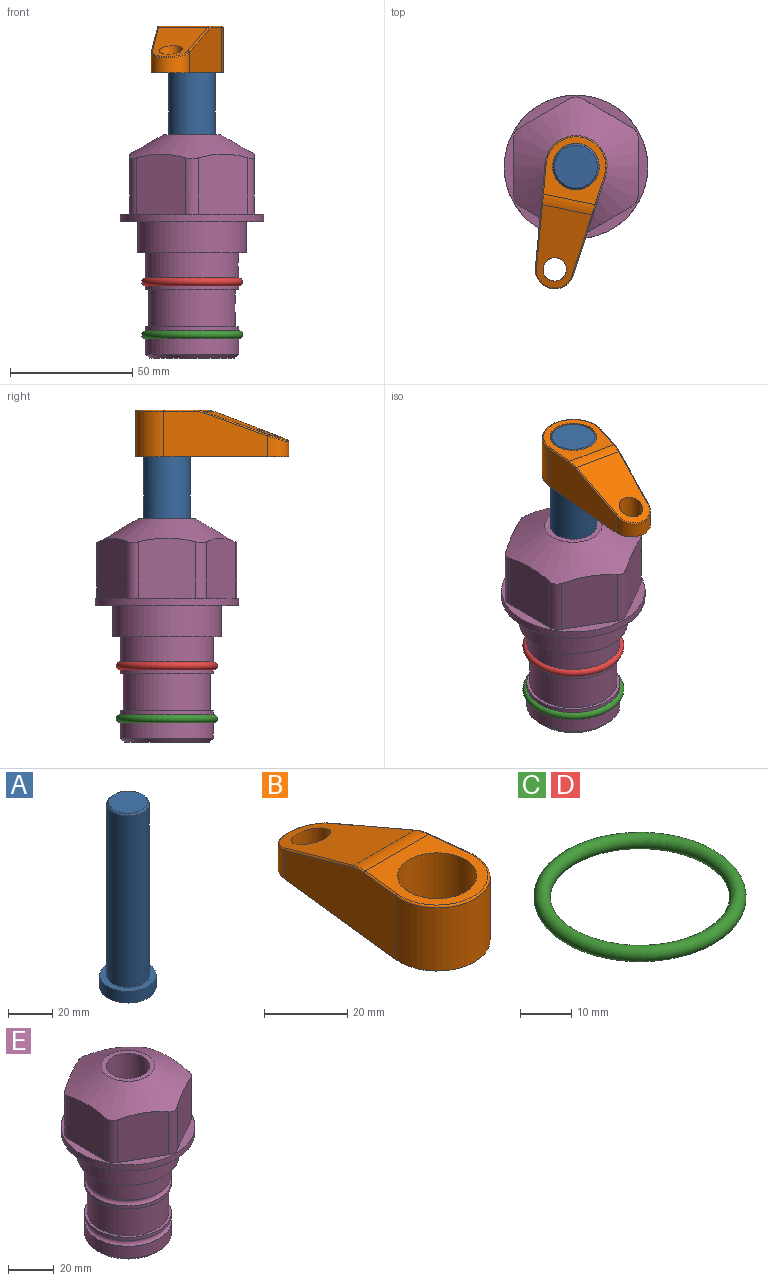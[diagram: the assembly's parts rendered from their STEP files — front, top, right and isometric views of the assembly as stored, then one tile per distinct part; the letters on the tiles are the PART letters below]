
ASSEMBLY  parts=5 mates=3
PART A: 6 faces, bbox 25.4x25.4x101.6 mm
  f0: plane 17.46x17.46mm, normal (0,0,1), area 239.5mm2, adj f5
  f1: plane 25.4x25.4mm, normal (0,0,-1), area 506.7mm2, adj f2
  f2: cylinder r=12.7mm len=25.4mm, axis (0,0,1), area 506.7mm2, adj f1,f3
  f3: plane 25.4x25.4mm, normal (0,0,1), area 221.7mm2, adj f2,f4
  f4: cylinder r=9.53mm len=94.46mm, axis (0,0,1), area 5653mm2, adj f3,f5
  f5: cone r=8.73mm half-angle=45deg, axis (0,0,-1), area 64.4mm2, adj f0,f4
PART B: 44 faces, bbox 27.5x64.5x19.1 mm
  f0: plane 2.3x0.95mm, normal (0,0,-1), area 1mm2, adj f25,f30,f34
  f1: plane 63.5x25.4mm, normal (0,0,-1), area 561.7mm2, adj f2,f3,f4,f5,f6,f7,f19,f20
  f2: cylinder r=12.7mm len=25.4mm, axis (0,0,-1), area 792.2mm2, adj f1,f3,f5,f13
  f3: plane 42.33x18.54mm, normal (0.99,0.11,0), area 647mm2, adj f1,f2,f4,f11,f12,f14
  f4: cylinder r=7.94mm len=15.78mm, axis (0,0,-1), area 158.6mm2, adj f1,f3,f5,f16
  f5: plane 42.33x18.54mm, normal (-0.99,0.11,0), area 647mm2, adj f1,f2,f4,f15,f17,f18
  f6: cylinder r=9.53mm len=19.05mm, axis (0,0,-1), area 1140.1mm2, adj f1,f8
  f7: cylinder r=4.76mm len=10.98mm, axis (0,0,-1), area 276.1mm2, adj f1,f9
  f8: plane 25.83x24.38mm, normal (0,0,1), area 262.2mm2, adj f6,f10,f11,f13,f15
  f9: plane 32.49x20.55mm, normal (0,0.34,0.94), area 489.9mm2, adj f7,f10,f14,f16,f18
  f10: cylinder r=12.7mm len=21.49mm, axis (-1,0,0), area 93.2mm2, adj f8,f9,f12,f17
  f11: cylinder r=0.51mm len=12.34mm, axis (0.11,-0.99,0), area 9.9mm2, adj f3,f8,f12,f13
  f12: bspline ~7.62x1.64mm, area 3.5mm2, adj f3,f10,f11,f14
  f13: torus R=12.19mm, axis (0,0,1), area 33.6mm2, adj f2,f8,f11,f15
  f14: cylinder r=0.51mm len=26.01mm, axis (0.1,-0.93,0.34), area 21.6mm2, adj f3,f9,f12,f16
  f15: cylinder r=0.51mm len=12.34mm, axis (0.11,0.99,0), area 9.9mm2, adj f5,f8,f13,f17
  f16: bspline ~15.78x7.05mm, area 15.7mm2, adj f4,f9,f14,f18
  f17: bspline ~7.62x1.64mm, area 3.5mm2, adj f5,f10,f15,f18
  f18: cylinder r=0.51mm len=26.01mm, axis (0.1,0.93,-0.34), area 21.6mm2, adj f5,f9,f16,f17
  f19: plane 21.6x14.29mm, normal (-0.99,-0.11,0), area 242.6mm2, adj f1,f26,f28,f34,f36,f38
  f20: plane 21.6x14.29mm, normal (0.99,-0.11,0), area 242.6mm2, adj f1,f27,f29,f37,f39,f41
  f21: cylinder r=12.7mm len=14.29mm, axis (0,0,-1), area 173.2mm2, adj f1,f26,f27,f30,f31,f33
  f22: cylinder r=7.94mm len=7.63mm, axis (0,0,-1), area 53.8mm2, adj f1,f28,f29,f42
  f23: plane 2.3x0.95mm, normal (0,0,-1), area 1mm2, adj f25,f33,f37
  f24: plane 17.94x12.32mm, normal (0,-0.34,-0.94), area 191.2mm2, adj f25,f38,f41,f42
  f25: cylinder r=9.53mm len=12.93mm, axis (-1,0,0), area 37.5mm2, adj f0,f23,f24,f31,f36,f39
  f26: cylinder r=1.59mm len=14.29mm, axis (0,0,-1), area 49mm2, adj f1,f19,f21,f32
  f27: cylinder r=1.59mm len=14.29mm, axis (0,0,-1), area 49mm2, adj f1,f20,f21,f35
  f28: cylinder r=1.59mm len=7.28mm, axis (0,0,-1), area 22.1mm2, adj f1,f19,f22,f40
  f29: cylinder r=1.59mm len=7.28mm, axis (0,0,-1), area 22.1mm2, adj f1,f20,f22,f43
  f30: torus R=14.29mm, axis (0,0,1), area 5.8mm2, adj f0,f21,f31,f32
  f31: bspline ~11.06x2.73mm, area 20.8mm2, adj f21,f25,f30,f33
  f32: sphere r=1.59mm, area 5.4mm2, adj f26,f30,f34
  f33: torus R=14.29mm, axis (0,0,1), area 5.8mm2, adj f21,f23,f31,f35
  f34: cylinder r=1.59mm len=1.68mm, axis (-0.11,0.99,0), area 2.4mm2, adj f0,f19,f32,f36
  f35: sphere r=1.59mm, area 5.4mm2, adj f27,f33,f37
  f36: bspline ~5.82x2.33mm, area 7.7mm2, adj f19,f25,f34,f38
  f37: cylinder r=1.59mm len=1.68mm, axis (0.11,0.99,0), area 2.4mm2, adj f20,f23,f35,f39
  f38: cylinder r=1.59mm len=18.33mm, axis (0.1,-0.93,0.34), area 46.7mm2, adj f19,f24,f36,f40
  f39: bspline ~5.82x2.33mm, area 7.7mm2, adj f20,f25,f37,f41
  f40: sphere r=1.59mm, area 3.6mm2, adj f28,f38,f42
  f41: cylinder r=1.59mm len=18.33mm, axis (0.1,0.93,-0.34), area 46.7mm2, adj f20,f24,f39,f43
  f42: bspline ~8.31x1.84mm, area 15.3mm2, adj f22,f24,f40,f43
  f43: sphere r=1.59mm, area 3.6mm2, adj f29,f41,f42
PART C: 1 faces, bbox 44.7x44.7x3.2 mm
  f0: torus R=19.05mm, axis (0,0,1), area 1193.9mm2
PART D: same geometry as C
PART E: 36 faces, bbox 58.7x58.7x91.2 mm
  f0: cylinder r=17.78mm len=35.56mm, axis (0,0,1), area 1670.8mm2, adj f23,f24,f31
  f1: cylinder r=19.05mm len=38.1mm, axis (0,0,1), area 1191.9mm2, adj f26,f27,f30
  f2: plane 58.66x58.66mm, normal (0,0,-1), area 1150.6mm2, adj f3,f28
  f3: cylinder r=29.33mm len=58.66mm, axis (0,0,-1), area 585.1mm2, adj f2,f4
  f4: plane 58.66x58.66mm, normal (0,0,1), area 475.9mm2, adj f3,f5,f6,f7,f8,f9,f10,f11
  f5: plane 24.5x20.32mm, normal (0.5,-0.87,0), area 562.8mm2, adj f4,f15,f16,f17
  f6: plane 24.5x20.32mm, normal (-0.5,-0.87,0), area 562.8mm2, adj f4,f14,f15,f17
  f7: plane 24.5x23.48mm, normal (-1,0,0), area 562.8mm2, adj f4,f13,f14,f17
  f8: plane 24.5x20.32mm, normal (-0.5,0.87,0), area 562.8mm2, adj f4,f12,f13,f17
  f9: plane 24.5x20.32mm, normal (0.5,0.87,0), area 562.8mm2, adj f4,f11,f12,f17
  f10: plane 24.5x23.48mm, normal (1,0,0), area 562.8mm2, adj f4,f11,f16,f17
  f11: cylinder r=5.08mm len=23.01mm, axis (0,0,-1), area 121.2mm2, adj f4,f9,f10,f17
  f12: cylinder r=5.08mm len=23.01mm, axis (0,0,-1), area 121.2mm2, adj f4,f8,f9,f17
  f13: cylinder r=5.08mm len=23.01mm, axis (0,0,-1), area 121.2mm2, adj f4,f7,f8,f17
  f14: cylinder r=5.08mm len=23.01mm, axis (0,0,-1), area 121.2mm2, adj f4,f6,f7,f17
  f15: cylinder r=5.08mm len=23.01mm, axis (0,0,-1), area 121.2mm2, adj f4,f5,f6,f17
  f16: cylinder r=5.08mm len=23.01mm, axis (0,0,-1), area 121.2mm2, adj f4,f5,f10,f17
  f17: cone r=11.73mm half-angle=60deg, axis (0,0,-1), area 2071.8mm2, adj f5,f6,f7,f8,f9,f10,f11,f12
  f18: plane 23.46x23.46mm, normal (0,0,1), area 147.4mm2, adj f17,f35
  f19: plane 34.93x34.93mm, normal (0,0,-1), area 958mm2, adj f29
  f20: cylinder r=19.05mm len=38.1mm, axis (0,0,1), area 760.1mm2, adj f21,f29
  f21: torus R=19.05mm, axis (0,0,1), area 565.3mm2, adj f20,f22
  f22: cylinder r=19.05mm len=38.1mm, axis (0,0,1), area 190mm2, adj f21,f23
  f23: plane 38.1x38.1mm, normal (0,0,1), area 146.9mm2, adj f0,f22
  f24: plane 38.1x38.1mm, normal (0,0,-1), area 146.9mm2, adj f0,f25
  f25: cylinder r=19.05mm len=38.1mm, axis (0,0,1), area 190mm2, adj f24,f26
  f26: torus R=19.05mm, axis (0,0,1), area 565.3mm2, adj f1,f25
  f27: plane 44.45x44.45mm, normal (0,0,-1), area 411.7mm2, adj f1,f28
  f28: cylinder r=22.23mm len=44.45mm, axis (0,0,1), area 1773.5mm2, adj f2,f27
  f29: cone r=19.05mm half-angle=45deg, axis (0,0,1), area 257.5mm2, adj f19,f20
  f30: cylinder r=3.17mm len=6.75mm, axis (-1,0,0), area 128mm2, adj f1,f33
  f31: cylinder r=3.17mm len=6.35mm, axis (-1,0,0), area 102.5mm2, adj f0,f33
  f32: plane 25.4x25.4mm, normal (0,0,1), area 506.7mm2, adj f33
  f33: cylinder r=12.7mm len=66.42mm, axis (0,0,-1), area 5236.2mm2, adj f30,f31,f32,f34
  f34: cone r=9.53mm half-angle=30deg, axis (0,0,-1), area 443.4mm2, adj f33,f35
  f35: cylinder r=9.53mm len=19.05mm, axis (0,0,-1), area 849mm2, adj f18,f34
PLACE A rot(axis=(0,0,-1),101.7deg) t=(0,0,6.38)mm
PLACE B rot(axis=(0,0,1),168.3deg) t=(0,0,60.99)mm
PLACE C t=(0,0,-21.59)mm
PLACE D at identity
PLACE E at identity fixed
MATE fastened C.f0 <-> E.f0  axis (0,0,1) through (0,0,-46.1)mm
MATE cylindrical A.f2 <-> E.f0  axis (0,0,1) through (0,0,32.01)mm
MATE fastened B.f2 <-> A.f2  axis (0,0,1) through (0,0,80.04)mm
